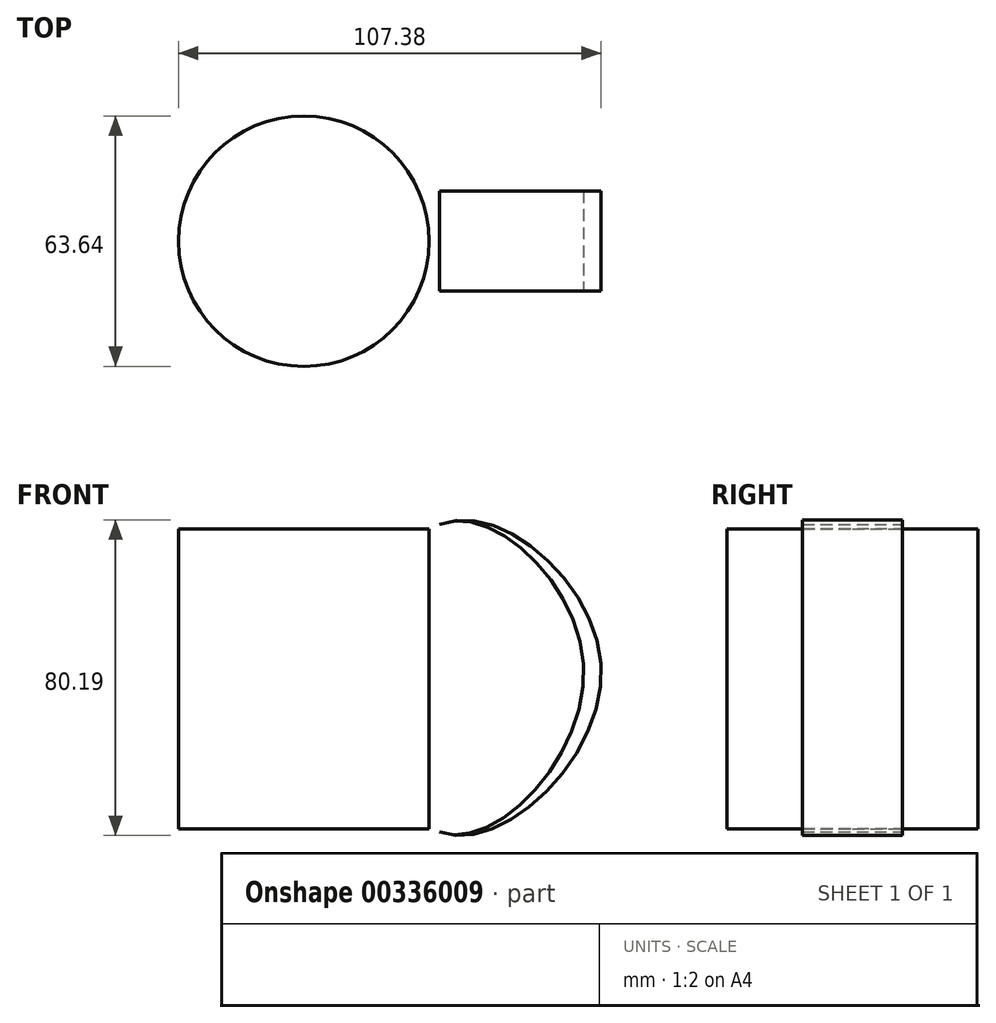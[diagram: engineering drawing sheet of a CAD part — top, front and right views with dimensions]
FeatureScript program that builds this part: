
annotation { "Feature Type Name" : "Feature", "Feature Type Description" : "" }
export const myFeature = defineFeature(function(context is Context, id is Id, definition is map)
    precondition{}
    {
        {
            var Q0;
            Q0=qCreatedBy(makeId("Top.planeOp"),FACE);
            var sketch = newSketch(context, id + "F0", { "sketchPlane" : qUnion([Q0])});
            skCircle(sketch, "E0", {"center": v(0, 0) * mm, "radius": 31.82 * mm});
            skSolve(sketch);
        }
        {
            var Q0;
            Q0=makeQuery(id+"F0.imprint","IMPRINT",FACE,{"disambiguationData":[TD([[makeQuery(id+"F0.imprint","IMPRINT",EDGE,{"derivedFrom":sQuery(id+"F0.wireOp",EDGE,"E0")}),1.0]])]});
            extrude(context, id + "F1", {"entities" : qUnion([Q0]), "depth" : 76.2 * mm});
        }
        {
            var Q0;
            Q0=qCreatedBy(makeId("Front.planeOp"),FACE);
            var sketch = newSketch(context, id + "F2", { "sketchPlane" : qUnion([Q0])});
            skFitSpline(sketch, "E1", {"points": [v(32.26, 76.19) * mm, v(75.55, 40.11) * mm, v(32.47, 0.21) * mm, v(32.26, 76.19) * mm]});
            skFitSpline(sketch, "E2", {"points": [v(32.47, 0.21) * mm, v(71.1, 40.15) * mm, v(32.26, 76.19) * mm, v(32.47, 0.21) * mm]});
            skSolve(sketch);
        }
        {
            var Q0;
            {var subQ0=sQuery(id+"F2.wireOp",EDGE,"E2");var subQ1=sQuery(id+"F2.wireOp",EDGE,"E1");var subQ2=makeQuery(id+"F2.imprint","INTERSECT",VERTEX,{"disambiguationData":[OD(0.0)],"derivedFrom":[subQ1,subQ0]});Q0=makeQuery(id+"F2.imprint","IMPRINT",FACE,{"disambiguationData":[TD([[makeQuery(id+"F2.imprint","IMPRINT",EDGE,{"disambiguationData":[TD([[subQ2,-1.0]])],"derivedFrom":subQ1}),-1.0]])]});}
            extrude(context, id + "F3", {"entities" : qUnion([Q0]), "endBound" : BoundingType.SYMMETRIC, "depth" : 25.4 * mm});
        }
    });
